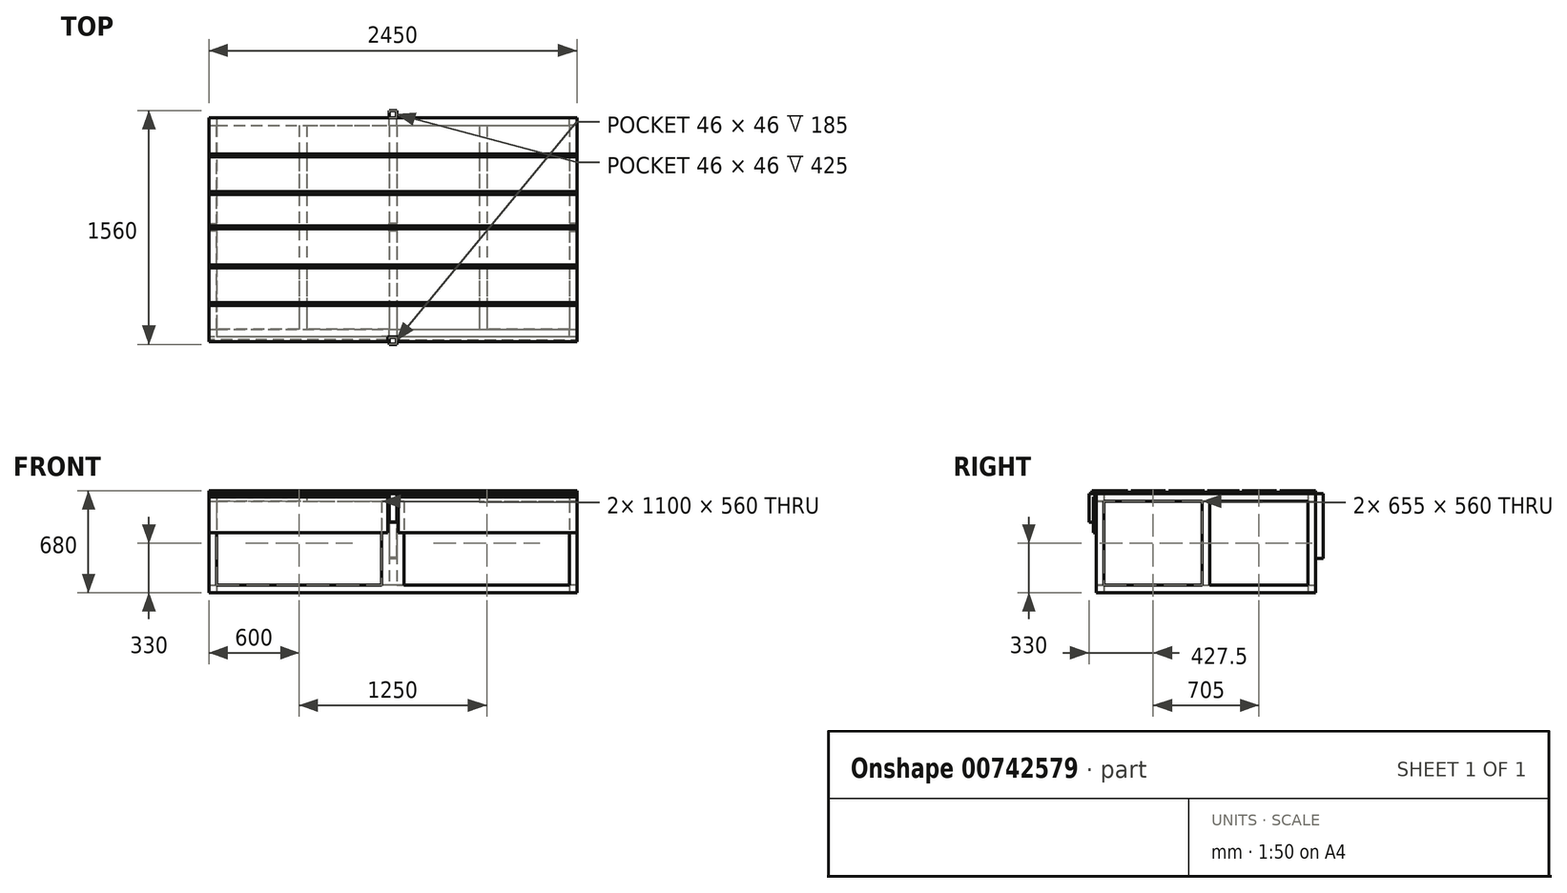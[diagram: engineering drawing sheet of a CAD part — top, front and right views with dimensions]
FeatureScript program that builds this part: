
annotation { "Feature Type Name" : "Feature", "Feature Type Description" : "" }
export const myFeature = defineFeature(function(context is Context, id is Id, definition is map)
    precondition{}
    {
        {
            var Q0;
            Q0=qCreatedBy(makeId("Top.planeOp"),FACE);
            var sketch = newSketch(context, id + "F0", { "sketchPlane" : qUnion([Q0])});
            skLineSegment(sketch, "E0.bottom", {"start": v(1225, -730) * mm, "end": v(-1225, -730) * mm});
            skLineSegment(sketch, "E0.top", {"start": v(1225, 730) * mm, "end": v(-1225, 730) * mm});
            skLineSegment(sketch, "E0.left", {"start": v(1225, -730) * mm, "end": v(1225, 730) * mm});
            skLineSegment(sketch, "E0.right", {"start": v(-1225, -730) * mm, "end": v(-1225, 730) * mm});
            skPoint(sketch, "E0.middle", {"position": v(0, 0) * mm});
            skLineSegment(sketch, "E1.bottom", {"start": v(-1175, 680) * mm, "end": v(1175, 680) * mm});
            skLineSegment(sketch, "E1.top", {"start": v(-1175, -680) * mm, "end": v(1175, -680) * mm});
            skLineSegment(sketch, "E1.left", {"start": v(-1175, 680) * mm, "end": v(-1175, -680) * mm});
            skLineSegment(sketch, "E1.right", {"start": v(1175, 680) * mm, "end": v(1175, -680) * mm});
            skLineSegment(sketch, "E2.bottom", {"start": v(25, 680) * mm, "end": v(-25, 680) * mm});
            skLineSegment(sketch, "E2.top", {"start": v(25, -680) * mm, "end": v(-25, -680) * mm});
            skLineSegment(sketch, "E2.left", {"start": v(25, 680) * mm, "end": v(25, -680) * mm});
            skLineSegment(sketch, "E2.right", {"start": v(-25, 680) * mm, "end": v(-25, -680) * mm});
            skSolve(sketch);
        }
        {
            var Q0;
            Q0=qSketchRegion(id+"F0",true);
            var Q1;
            Q1=makeQuery(id+"F0.imprint","IMPRINT",FACE,{"disambiguationData":[TD([[makeQuery(id+"F0.imprint","IMPRINT",EDGE,{"derivedFrom":sQuery(id+"F0.wireOp",EDGE,"E2.bottom")}),1.0]])]});
            extrude(context, id + "F1", {"entities" : qUnion([Q0, Q1]), "depth" : 50 * mm, "offsetDistance" : 25 * mm});
        }
        {
            var Q0;
            Q0=makeQuery(id+"F1.opExtrude","CAP_FACE",FACE,{"disambiguationData":[OSD([sQuery(id+"F0.wireOp",EDGE,"E0.bottom"),sQuery(id+"F0.wireOp",EDGE,"E0.top"),sQuery(id+"F0.wireOp",EDGE,"E0.left"),sQuery(id+"F0.wireOp",EDGE,"E0.right"),sQuery(id+"F0.wireOp",EDGE,"E1.bottom"),sQuery(id+"F0.wireOp",EDGE,"E1.top"),sQuery(id+"F0.wireOp",EDGE,"E1.left"),sQuery(id+"F0.wireOp",EDGE,"E1.right"),sQuery(id+"F0.wireOp",EDGE,"E2.left"),sQuery(id+"F0.wireOp",EDGE,"E2.right")])],"isStart":false});
            var sketch = newSketch(context, id + "F2", { "sketchPlane" : qUnion([Q0])});
            skLineSegment(sketch, "E3.bottom", {"start": v(-1225, 730) * mm, "end": v(-1175, 730) * mm});
            skLineSegment(sketch, "E3.top", {"start": v(-1225, 680) * mm, "end": v(-1175, 680) * mm});
            skLineSegment(sketch, "E3.left", {"start": v(-1225, 730) * mm, "end": v(-1225, 680) * mm});
            skLineSegment(sketch, "E3.right", {"start": v(-1175, 730) * mm, "end": v(-1175, 680) * mm});
            skLineSegment(sketch, "E4", {"start": v(-25, 680) * mm, "end": v(-25, 730) * mm});
            skLineSegment(sketch, "E5", {"start": v(25, 680) * mm, "end": v(25, 730) * mm});
            skLineSegment(sketch, "E6", {"start": v(25, 730) * mm, "end": v(-25, 730) * mm});
            skLineSegment(sketch, "E7", {"start": v(-25, 680) * mm, "end": v(25, 680) * mm});
            skLineSegment(sketch, "E8", {"start": v(1175, 680) * mm, "end": v(1175, 730) * mm});
            skLineSegment(sketch, "E9", {"start": v(1175, 730) * mm, "end": v(1225, 730) * mm});
            skLineSegment(sketch, "E10", {"start": v(1225, 730) * mm, "end": v(1225, 680) * mm});
            skLineSegment(sketch, "E11", {"start": v(1225, 680) * mm, "end": v(1175, 680) * mm});
            skLineSegment(sketch, "E12", {"start": v(1175, -680) * mm, "end": v(1225, -680) * mm});
            skLineSegment(sketch, "E13", {"start": v(1225, -680) * mm, "end": v(1225, -730) * mm});
            skLineSegment(sketch, "E14", {"start": v(1225, -730) * mm, "end": v(1175, -730) * mm});
            skLineSegment(sketch, "E15", {"start": v(1175, -730) * mm, "end": v(1175, -680) * mm});
            skLineSegment(sketch, "E16", {"start": v(-25, -680) * mm, "end": v(25, -680) * mm});
            skLineSegment(sketch, "E17", {"start": v(25, -680) * mm, "end": v(25, -730) * mm});
            skLineSegment(sketch, "E18", {"start": v(25, -730) * mm, "end": v(-25, -730) * mm});
            skLineSegment(sketch, "E19", {"start": v(-25, -730) * mm, "end": v(-25, -680) * mm});
            skLineSegment(sketch, "E20", {"start": v(-1175, -680) * mm, "end": v(-1175, -730) * mm});
            skLineSegment(sketch, "E21", {"start": v(-1175, -730) * mm, "end": v(-1225, -730) * mm});
            skLineSegment(sketch, "E22", {"start": v(-1225, -730) * mm, "end": v(-1225, -680) * mm});
            skLineSegment(sketch, "E23", {"start": v(-1225, -680) * mm, "end": v(-1175, -680) * mm});
            skLineSegment(sketch, "E24.bottom", {"start": v(25, -25) * mm, "end": v(-25, -25) * mm});
            skLineSegment(sketch, "E24.top", {"start": v(25, 25) * mm, "end": v(-25, 25) * mm});
            skLineSegment(sketch, "E24.left", {"start": v(25, -25) * mm, "end": v(25, 25) * mm});
            skLineSegment(sketch, "E24.right", {"start": v(-25, -25) * mm, "end": v(-25, 25) * mm});
            skPoint(sketch, "E24.middle", {"position": v(0, 0) * mm});
            skLineSegment(sketch, "E25", {"start": v(0, 0) * mm, "end": v(-1225, 0) * mm});
            skLineSegment(sketch, "E26", {"start": v(-1225, 25) * mm, "end": v(-1175, 25) * mm});
            skLineSegment(sketch, "E27", {"start": v(-1175, 25) * mm, "end": v(-1175, -25) * mm});
            skLineSegment(sketch, "E28", {"start": v(-1175, -25) * mm, "end": v(-1225, -25) * mm});
            skLineSegment(sketch, "E29", {"start": v(-1225, 25) * mm, "end": v(-1225, -25) * mm});
            skLineSegment(sketch, "E30.MirrorCS", {"start": v(1225, 25) * mm, "end": v(1225, -25) * mm});
            skLineSegment(sketch, "E31.MirrorCS", {"start": v(1175, -25) * mm, "end": v(1225, -25) * mm});
            skLineSegment(sketch, "E32.MirrorCS", {"start": v(1225, 25) * mm, "end": v(1175, 25) * mm});
            skLineSegment(sketch, "E33.MirrorCS", {"start": v(1175, 25) * mm, "end": v(1175, -25) * mm});
            skSolve(sketch);
        }
        {
            var Q0;
            Q0=qSketchRegion(id+"F2",true);
            extrude(context, id + "F3", {"entities" : qUnion([Q0]), "operationType" : NewBodyOperationType.ADD, "depth" : 560 * mm, "offsetDistance" : 25 * mm});
        }
        {
            var Q0;
            Q0=makeQuery(id+"F3.opExtrude","CAP_FACE",FACE,{"disambiguationData":[OSD([sQuery(id+"F2.wireOp",EDGE,"E26"),sQuery(id+"F2.wireOp",EDGE,"E27"),sQuery(id+"F2.wireOp",EDGE,"E28"),sQuery(id+"F2.wireOp",EDGE,"E29")])],"isStart":false});
            var sketch = newSketch(context, id + "F4", { "sketchPlane" : qUnion([Q0])});
            skLineSegment(sketch, "E34", {"start": v(-1225, 25) * mm, "end": v(-1225, 730) * mm});
            skLineSegment(sketch, "E35", {"start": v(-1225, 730) * mm, "end": v(-1175, 730) * mm});
            skLineSegment(sketch, "E36", {"start": v(-1175, 730) * mm, "end": v(1225, 730) * mm});
            skLineSegment(sketch, "E37", {"start": v(1225, 730) * mm, "end": v(1225, -730) * mm});
            skLineSegment(sketch, "E38", {"start": v(1225, -730) * mm, "end": v(-1225, -730) * mm});
            skLineSegment(sketch, "E39", {"start": v(-1225, -730) * mm, "end": v(-1225, 25) * mm});
            skLineSegment(sketch, "E40", {"start": v(-1175, 730) * mm, "end": v(-1175, 680) * mm});
            skLineSegment(sketch, "E41", {"start": v(-1175, 680) * mm, "end": v(-25, 680) * mm});
            skLineSegment(sketch, "E42", {"start": v(-1175, 680) * mm, "end": v(-600, 680) * mm});
            skLineSegment(sketch, "E43", {"start": v(-600, 680) * mm, "end": v(-575, 680) * mm});
            skLineSegment(sketch, "E44", {"start": v(-600, 680) * mm, "end": v(-625, 680) * mm});
            skLineSegment(sketch, "E45", {"start": v(-625, 680) * mm, "end": v(-625, -680) * mm});
            skLineSegment(sketch, "E46.MirrorCS", {"start": v(-575, 680) * mm, "end": v(-575, -680) * mm});
            skLineSegment(sketch, "E47", {"start": v(-25, 680) * mm, "end": v(25, 680) * mm});
            skLineSegment(sketch, "E48", {"start": v(25, 680) * mm, "end": v(1175, 680) * mm});
            skLineSegment(sketch, "E49", {"start": v(25, 680) * mm, "end": v(600, 680) * mm});
            skLineSegment(sketch, "E50", {"start": v(600, 680) * mm, "end": v(575, 680) * mm});
            skLineSegment(sketch, "E51", {"start": v(575, 680) * mm, "end": v(575, -680) * mm});
            skLineSegment(sketch, "E52.MirrorCS", {"start": v(625, 680) * mm, "end": v(625, -680) * mm});
            skLineSegment(sketch, "E53", {"start": v(-25, 680) * mm, "end": v(-25, -680) * mm});
            skLineSegment(sketch, "E54", {"start": v(-25, -680) * mm, "end": v(-575, -680) * mm});
            skLineSegment(sketch, "E55", {"start": v(-625, -680) * mm, "end": v(-1175, -680) * mm});
            skLineSegment(sketch, "E56", {"start": v(-1175, -680) * mm, "end": v(-1175, 680) * mm});
            skLineSegment(sketch, "E57", {"start": v(1175, 680) * mm, "end": v(1175, -680) * mm});
            skLineSegment(sketch, "E58", {"start": v(1175, -680) * mm, "end": v(625, -680) * mm});
            skLineSegment(sketch, "E59", {"start": v(25, 680) * mm, "end": v(25, -680) * mm});
            skLineSegment(sketch, "E60", {"start": v(25, -680) * mm, "end": v(575, -680) * mm});
            skSolve(sketch);
        }
        {
            var Q0;
            Q0=qSketchRegion(id+"F4",true);
            extrude(context, id + "F5", {"entities" : qUnion([Q0]), "operationType" : NewBodyOperationType.ADD, "depth" : 50 * mm, "offsetDistance" : 25 * mm});
        }
        {
            var Q0;
            {var subQ5=sQuery(id+"F0.wireOp",EDGE,"E1.left");var subQ6=sQuery(id+"F0.wireOp",EDGE,"E1.top");var subQ8=makeQuery(id+"F1.opExtrude","CAP_EDGE",EDGE,{"disambiguationData":[OSD([subQ6]),TDD([makeQuery(id+"F0.imprint","IMPRINT",EDGE,{"disambiguationData":[TD([[makeQuery(id+"F0.imprint","INTERSECT",VERTEX,{"derivedFrom":[subQ6,subQ5]}),-1.0]])],"derivedFrom":subQ6})])],"isStart":false});Q0=makeQuery(id+"F2.imprint","IMPRINT",FACE,{"disambiguationData":[TD([[makeQuery(id+"F2.imprint","IMPRINT",EDGE,{"derivedFrom":subQ8}),1.0]])]});}
            cPlane(context, id + "F6", {"entities" : qUnion([Q0]), "cplaneType" : CPlaneType.OFFSET, "offset" : 420 * mm, "width" : 150 * mm, "height" : 150 * mm});
        }
        {
            var Q0;
            Q0=qCreatedBy(id+"F6.planeOp",FACE);
            var sketch = newSketch(context, id + "F7", { "sketchPlane" : qUnion([Q0])});
            skLineSegment(sketch, "E61.bottom", {"start": v(-25, -730) * mm, "end": v(25, -730) * mm});
            skLineSegment(sketch, "E61.top", {"start": v(-25, -780) * mm, "end": v(25, -780) * mm});
            skLineSegment(sketch, "E61.left", {"start": v(-25, -730) * mm, "end": v(-25, -780) * mm});
            skLineSegment(sketch, "E61.right", {"start": v(25, -730) * mm, "end": v(25, -780) * mm});
            skSolve(sketch);
        }
        {
            var Q0;
            Q0=qSketchRegion(id+"F7",true);
            extrude(context, id + "F8", {"entities" : qUnion([Q0]), "operationType" : NewBodyOperationType.ADD, "depth" : 5 * mm, "offsetDistance" : 25 * mm});
        }
        {
            var Q0;
            Q0=makeQuery(id+"F8.opExtrude","CAP_FACE",FACE,{"disambiguationData":[OSD([sQuery(id+"F7.wireOp",EDGE,"E61.bottom"),sQuery(id+"F7.wireOp",EDGE,"E61.top"),sQuery(id+"F7.wireOp",EDGE,"E61.left"),sQuery(id+"F7.wireOp",EDGE,"E61.right")])],"isStart":false});
            var sketch = newSketch(context, id + "F9", { "sketchPlane" : qUnion([Q0])});
            skLineSegment(sketch, "E62.bottom", {"start": v(-25, -730) * mm, "end": v(25, -730) * mm});
            skLineSegment(sketch, "E62.top", {"start": v(-25, -780) * mm, "end": v(25, -780) * mm});
            skLineSegment(sketch, "E62.left", {"start": v(-25, -730) * mm, "end": v(-25, -780) * mm});
            skLineSegment(sketch, "E62.right", {"start": v(25, -730) * mm, "end": v(25, -780) * mm});
            skLineSegment(sketch, "E63.bottom", {"start": v(25, -780) * mm, "end": v(23, -780) * mm});
            skLineSegment(sketch, "E63.top", {"start": v(25, -778) * mm, "end": v(23, -778) * mm});
            skLineSegment(sketch, "E63.left", {"start": v(25, -780) * mm, "end": v(25, -778) * mm});
            skLineSegment(sketch, "E63.right", {"start": v(23, -780) * mm, "end": v(23, -778) * mm});
            skLineSegment(sketch, "E64.bottom", {"start": v(23, -778) * mm, "end": v(-23, -778) * mm});
            skLineSegment(sketch, "E64.top", {"start": v(23, -732) * mm, "end": v(-23, -732) * mm});
            skLineSegment(sketch, "E64.left", {"start": v(23, -778) * mm, "end": v(23, -732) * mm});
            skLineSegment(sketch, "E64.right", {"start": v(-23, -778) * mm, "end": v(-23, -732) * mm});
            skSolve(sketch);
        }
        {
            var Q0;
            Q0=qSketchRegion(id+"F9",true);
            var Q1;
            {var subQ0=sQuery(id+"F4.wireOp",EDGE,"E60");var subQ1=sQuery(id+"F4.wireOp",EDGE,"E59");var subQ2=sQuery(id+"F4.wireOp",EDGE,"E58");var subQ3=sQuery(id+"F4.wireOp",EDGE,"E57");var subQ4=sQuery(id+"F4.wireOp",EDGE,"E56");var subQ5=sQuery(id+"F4.wireOp",EDGE,"E55");var subQ6=sQuery(id+"F4.wireOp",EDGE,"E54");var subQ7=sQuery(id+"F4.wireOp",EDGE,"E53");var subQ8=sQuery(id+"F4.wireOp",EDGE,"E52.MirrorCS");var subQ9=sQuery(id+"F4.wireOp",EDGE,"E51");var subQ10=sQuery(id+"F4.wireOp",EDGE,"E49");var subQ11=sQuery(id+"F4.wireOp",EDGE,"E48");var subQ12=sQuery(id+"F4.wireOp",EDGE,"E46.MirrorCS");var subQ13=sQuery(id+"F4.wireOp",EDGE,"E45");var subQ14=sQuery(id+"F4.wireOp",EDGE,"E42");var subQ15=sQuery(id+"F4.wireOp",EDGE,"E41");var subQ16=sQuery(id+"F4.wireOp",EDGE,"E39");var subQ17=sQuery(id+"F4.wireOp",EDGE,"E38");var subQ18=sQuery(id+"F4.wireOp",EDGE,"E37");var subQ19=sQuery(id+"F4.wireOp",EDGE,"E36");var subQ20=sQuery(id+"F4.wireOp",EDGE,"E35");var subQ21=sQuery(id+"F4.wireOp",EDGE,"E34");Q1=makeQuery(id+"FP4IzDu3Lu8PIDH_1.boolean.opBoolean","MERGE",FACE,{"derivedFrom":[makeQuery(id+"F5.opExtrude","CAP_FACE",FACE,{"disambiguationData":[OSD([subQ21,subQ20,subQ19,subQ18,subQ17,subQ16,subQ15,subQ14,subQ13,subQ12,subQ11,subQ10,subQ9,subQ8,subQ7,subQ6,subQ5,subQ4,subQ3,subQ2,subQ1,subQ0])],"isStart":false}),makeQuery(id+"FP4IzDu3Lu8PIDH_1.opExtrude","CAP_FACE",FACE,{"disambiguationData":[OSD([subQ21,subQ20,subQ19,subQ18,subQ17,subQ16,subQ15,subQ14,subQ13,subQ12,subQ11,subQ10,subQ9,subQ8,subQ7,subQ6,subQ5,subQ4,subQ3,subQ2,subQ1,subQ0])],"isStart":false})]});}
            extrude(context, id + "F10", {"entities" : qUnion([Q0]), "operationType" : NewBodyOperationType.ADD, "endBound" : BoundingType.UP_TO_SURFACE, "depth" : 25 * mm, "endBoundEntityFace" : qUnion([Q1]), "offsetDistance" : 25 * mm});
        }
        {
            var Q0;
            {var subQ5=sQuery(id+"F0.wireOp",EDGE,"E1.left");var subQ6=sQuery(id+"F0.wireOp",EDGE,"E1.top");var subQ8=makeQuery(id+"F1.opExtrude","CAP_EDGE",EDGE,{"disambiguationData":[OSD([subQ6]),TDD([makeQuery(id+"F0.imprint","IMPRINT",EDGE,{"disambiguationData":[TD([[makeQuery(id+"F0.imprint","INTERSECT",VERTEX,{"derivedFrom":[subQ6,subQ5]}),-1.0]])],"derivedFrom":subQ6})])],"isStart":false});Q0=makeQuery(id+"F2.imprint","IMPRINT",FACE,{"disambiguationData":[TD([[makeQuery(id+"F2.imprint","IMPRINT",EDGE,{"derivedFrom":subQ8}),1.0]])]});}
            cPlane(context, id + "F11", {"entities" : qUnion([Q0]), "cplaneType" : CPlaneType.OFFSET, "offset" : 180 * mm, "width" : 150 * mm, "height" : 150 * mm});
        }
        {
            var Q0;
            Q0=qCreatedBy(id+"F11.planeOp",FACE);
            var sketch = newSketch(context, id + "F12", { "sketchPlane" : qUnion([Q0])});
            skLineSegment(sketch, "E65.bottom", {"start": v(-25, 730) * mm, "end": v(25, 730) * mm});
            skLineSegment(sketch, "E65.top", {"start": v(-25, 780) * mm, "end": v(25, 780) * mm});
            skLineSegment(sketch, "E65.left", {"start": v(-25, 730) * mm, "end": v(-25, 780) * mm});
            skLineSegment(sketch, "E65.right", {"start": v(25, 730) * mm, "end": v(25, 780) * mm});
            skSolve(sketch);
        }
        {
            var Q0;
            Q0=makeQuery(id+"F12.imprint","IMPRINT",FACE,{"disambiguationData":[TD([[makeQuery(id+"F12.imprint","IMPRINT",EDGE,{"derivedFrom":sQuery(id+"F12.wireOp",EDGE,"E65.bottom")}),1.0]])]});
            extrude(context, id + "F13", {"entities" : qUnion([Q0]), "operationType" : NewBodyOperationType.ADD, "depth" : 5 * mm, "offsetDistance" : 25 * mm});
        }
        {
            var Q0;
            Q0=makeQuery(id+"F3.opExtrude","SWEPT_FACE",FACE,{"disambiguationData":[OSD([sQuery(id+"F2.wireOp",EDGE,"E17")])]});
            cPlane(context, id + "F14", {"entities" : qUnion([Q0]), "cplaneType" : CPlaneType.OFFSET, "offset" : 25 * mm, "oppositeDirection" : true, "width" : 150 * mm, "height" : 150 * mm});
        }
        {
            var Q0;
            Q0=qCreatedBy(id+"F14.planeOp",FACE);
            var sketch = newSketch(context, id + "F15", { "sketchPlane" : qUnion([Q0])});
            skLineSegment(sketch, "E66.bottom", {"start": v(-730, 610) * mm, "end": v(-725, 610) * mm});
            skLineSegment(sketch, "E66.top", {"start": v(-730, 50) * mm, "end": v(-725, 50) * mm});
            skLineSegment(sketch, "E66.left", {"start": v(-730, 610) * mm, "end": v(-730, 50) * mm});
            skLineSegment(sketch, "E66.right", {"start": v(-725, 610) * mm, "end": v(-725, 50) * mm});
            skLineSegment(sketch, "E67.bottom", {"start": v(730, 610) * mm, "end": v(725, 610) * mm});
            skLineSegment(sketch, "E67.top", {"start": v(730, 50) * mm, "end": v(725, 50) * mm});
            skLineSegment(sketch, "E67.left", {"start": v(730, 610) * mm, "end": v(730, 50) * mm});
            skLineSegment(sketch, "E67.right", {"start": v(725, 610) * mm, "end": v(725, 50) * mm});
            skSolve(sketch);
        }
        {
            var Q0;
            Q0=qSketchRegion(id+"F15",true);
            extrude(context, id + "F16", {"entities" : qUnion([Q0]), "operationType" : NewBodyOperationType.ADD, "depth" : 75 * mm, "offsetDistance" : 25 * mm, "hasSecondDirection" : true, "secondDirectionOppositeDirection" : true, "secondDirectionDepth" : 75 * mm});
        }
        {
            var Q0;
            Q0=makeQuery(id+"F13.opExtrude","CAP_FACE",FACE,{"disambiguationData":[OSD([sQuery(id+"F12.wireOp",EDGE,"E65.bottom"),sQuery(id+"F12.wireOp",EDGE,"E65.top"),sQuery(id+"F12.wireOp",EDGE,"E65.left"),sQuery(id+"F12.wireOp",EDGE,"E65.right")])],"isStart":false});
            var sketch = newSketch(context, id + "F17", { "sketchPlane" : qUnion([Q0])});
            skLineSegment(sketch, "E68.bottom", {"start": v(-25, 780) * mm, "end": v(25, 780) * mm});
            skLineSegment(sketch, "E68.top", {"start": v(-25, 730) * mm, "end": v(25, 730) * mm});
            skLineSegment(sketch, "E68.left", {"start": v(-25, 780) * mm, "end": v(-25, 730) * mm});
            skLineSegment(sketch, "E68.right", {"start": v(25, 780) * mm, "end": v(25, 730) * mm});
            skLineSegment(sketch, "E69.bottom", {"start": v(25, 730) * mm, "end": v(23, 730) * mm});
            skLineSegment(sketch, "E69.top", {"start": v(25, 732) * mm, "end": v(23, 732) * mm});
            skLineSegment(sketch, "E69.left", {"start": v(25, 730) * mm, "end": v(25, 732) * mm});
            skLineSegment(sketch, "E70.bottom", {"start": v(23, 732) * mm, "end": v(-23, 732) * mm});
            skLineSegment(sketch, "E70.top", {"start": v(23, 778) * mm, "end": v(-23, 778) * mm});
            skLineSegment(sketch, "E70.left", {"start": v(23, 732) * mm, "end": v(23, 778) * mm});
            skLineSegment(sketch, "E70.right", {"start": v(-23, 732) * mm, "end": v(-23, 778) * mm});
            skSolve(sketch);
        }
        {
            var Q0;
            Q0=qSketchRegion(id+"F17",true);
            var Q1;
            {var subQ0=sQuery(id+"F4.wireOp",EDGE,"E60");var subQ1=sQuery(id+"F4.wireOp",EDGE,"E59");var subQ2=sQuery(id+"F4.wireOp",EDGE,"E58");var subQ3=sQuery(id+"F4.wireOp",EDGE,"E57");var subQ4=sQuery(id+"F4.wireOp",EDGE,"E56");var subQ5=sQuery(id+"F4.wireOp",EDGE,"E55");var subQ6=sQuery(id+"F4.wireOp",EDGE,"E54");var subQ7=sQuery(id+"F4.wireOp",EDGE,"E53");var subQ8=sQuery(id+"F4.wireOp",EDGE,"E52.MirrorCS");var subQ9=sQuery(id+"F4.wireOp",EDGE,"E51");var subQ10=sQuery(id+"F4.wireOp",EDGE,"E49");var subQ11=sQuery(id+"F4.wireOp",EDGE,"E48");var subQ12=sQuery(id+"F4.wireOp",EDGE,"E46.MirrorCS");var subQ13=sQuery(id+"F4.wireOp",EDGE,"E45");var subQ14=sQuery(id+"F4.wireOp",EDGE,"E42");var subQ15=sQuery(id+"F4.wireOp",EDGE,"E41");var subQ16=sQuery(id+"F4.wireOp",EDGE,"E39");var subQ17=sQuery(id+"F4.wireOp",EDGE,"E38");var subQ18=sQuery(id+"F4.wireOp",EDGE,"E37");var subQ19=sQuery(id+"F4.wireOp",EDGE,"E36");var subQ20=sQuery(id+"F4.wireOp",EDGE,"E35");var subQ21=sQuery(id+"F4.wireOp",EDGE,"E34");Q1=makeQuery(id+"F10.boolean.opBoolean","MERGE",FACE,{"derivedFrom":[makeQuery(id+"F5.opExtrude","CAP_FACE",FACE,{"disambiguationData":[OSD([subQ21,subQ20,subQ19,subQ18,subQ17,subQ16,subQ15,subQ14,subQ13,subQ12,subQ11,subQ10,subQ9,subQ8,subQ7,subQ6,subQ5,subQ4,subQ3,subQ2,subQ1,subQ0])],"isStart":false}),makeQuery(id+"F10.opExtrude","CAP_FACE",FACE,{"disambiguationData":[OSD([subQ21,subQ20,subQ19,subQ18,subQ17,subQ16,subQ15,subQ14,subQ13,subQ12,subQ11,subQ10,subQ9,subQ8,subQ7,subQ6,subQ5,subQ4,subQ3,subQ2,subQ1,subQ0])],"isStart":false})]});}
            extrude(context, id + "F18", {"entities" : qUnion([Q0]), "operationType" : NewBodyOperationType.ADD, "endBound" : BoundingType.UP_TO_SURFACE, "depth" : 25 * mm, "endBoundEntityFace" : qUnion([Q1]), "offsetDistance" : 25 * mm});
        }
        {
            var Q0;
            {var subQ0=sQuery(id+"F4.wireOp",EDGE,"E60");var subQ1=sQuery(id+"F4.wireOp",EDGE,"E59");var subQ2=sQuery(id+"F4.wireOp",EDGE,"E58");var subQ3=sQuery(id+"F4.wireOp",EDGE,"E57");var subQ4=sQuery(id+"F4.wireOp",EDGE,"E56");var subQ5=sQuery(id+"F4.wireOp",EDGE,"E55");var subQ6=sQuery(id+"F4.wireOp",EDGE,"E54");var subQ7=sQuery(id+"F4.wireOp",EDGE,"E53");var subQ8=sQuery(id+"F4.wireOp",EDGE,"E52.MirrorCS");var subQ9=sQuery(id+"F4.wireOp",EDGE,"E51");var subQ10=sQuery(id+"F4.wireOp",EDGE,"E49");var subQ11=sQuery(id+"F4.wireOp",EDGE,"E48");var subQ12=sQuery(id+"F4.wireOp",EDGE,"E46.MirrorCS");var subQ13=sQuery(id+"F4.wireOp",EDGE,"E45");var subQ14=sQuery(id+"F4.wireOp",EDGE,"E42");var subQ15=sQuery(id+"F4.wireOp",EDGE,"E41");var subQ16=sQuery(id+"F4.wireOp",EDGE,"E39");var subQ17=sQuery(id+"F4.wireOp",EDGE,"E38");var subQ18=sQuery(id+"F4.wireOp",EDGE,"E37");var subQ19=sQuery(id+"F4.wireOp",EDGE,"E36");var subQ20=sQuery(id+"F4.wireOp",EDGE,"E35");var subQ21=sQuery(id+"F4.wireOp",EDGE,"E34");Q0=makeQuery(id+"F18.boolean.opBoolean","MERGE",FACE,{"derivedFrom":[makeQuery(id+"F10.boolean.opBoolean","MERGE",FACE,{"derivedFrom":[makeQuery(id+"F5.opExtrude","CAP_FACE",FACE,{"disambiguationData":[OSD([subQ21,subQ20,subQ19,subQ18,subQ17,subQ16,subQ15,subQ14,subQ13,subQ12,subQ11,subQ10,subQ9,subQ8,subQ7,subQ6,subQ5,subQ4,subQ3,subQ2,subQ1,subQ0])],"isStart":false}),makeQuery(id+"F10.opExtrude","CAP_FACE",FACE,{"disambiguationData":[OSD([subQ21,subQ20,subQ19,subQ18,subQ17,subQ16,subQ15,subQ14,subQ13,subQ12,subQ11,subQ10,subQ9,subQ8,subQ7,subQ6,subQ5,subQ4,subQ3,subQ2,subQ1,subQ0])],"isStart":false})]}),makeQuery(id+"F18.opExtrude","CAP_FACE",FACE,{"disambiguationData":[OSD([subQ21,subQ20,subQ19,subQ18,subQ17,subQ16,subQ15,subQ14,subQ13,subQ12,subQ11,subQ10,subQ9,subQ8,subQ7,subQ6,subQ5,subQ4,subQ3,subQ2,subQ1,subQ0])],"isStart":false})]});}
            var sketch = newSketch(context, id + "F19", { "sketchPlane" : qUnion([Q0])});
            skLineSegment(sketch, "E71.bottom", {"start": v(-1225, 730) * mm, "end": v(1225, 730) * mm});
            skLineSegment(sketch, "E71.top", {"start": v(-1225, -730) * mm, "end": v(1225, -730) * mm});
            skLineSegment(sketch, "E71.left", {"start": v(-1225, 730) * mm, "end": v(-1225, -730) * mm});
            skLineSegment(sketch, "E71.right", {"start": v(1225, 730) * mm, "end": v(1225, -730) * mm});
            skLineSegment(sketch, "E72", {"start": v(1225, -730) * mm, "end": v(1225, -760) * mm});
            skLineSegment(sketch, "E73.top", {"start": v(1225, -730) * mm, "end": v(46.2, -730) * mm});
            skLineSegment(sketch, "E73.left", {"start": v(1225, -760) * mm, "end": v(1225, -730) * mm});
            skLineSegment(sketch, "E74.top", {"start": v(46.2, -730) * mm, "end": v(-45, -730) * mm});
            skLineSegment(sketch, "E75.top", {"start": v(-45, -730) * mm, "end": v(-1225, -730) * mm});
            skLineSegment(sketch, "E75.right", {"start": v(-1225, -760) * mm, "end": v(-1225, -730) * mm});
            skLineSegment(sketch, "E76", {"start": v(35, -760) * mm, "end": v(35, -730) * mm});
            skLineSegment(sketch, "E77", {"start": v(-35, -760) * mm, "end": v(-35, -730) * mm});
            skLineSegment(sketch, "E78", {"start": v(35, -760) * mm, "end": v(1225, -760) * mm});
            skLineSegment(sketch, "E79", {"start": v(-1225, -760) * mm, "end": v(-35, -760) * mm});
            skSolve(sketch);
        }
        {
            var Q0;
            Q0=qSketchRegion(id+"F19",true);
            extrude(context, id + "F20", {"entities" : qUnion([Q0]), "depth" : 20 * mm, "offsetDistance" : 25 * mm});
        }
        {
            var Q0;
            Q0=makeQuery(id+"F16.boolean.opBoolean","MERGE",FACE,{"derivedFrom":[makeQuery(id+"F5.boolean.opBoolean","MERGE",FACE,{"derivedFrom":[makeQuery(id+"F3.boolean.opBoolean","MERGE",FACE,{"derivedFrom":[makeQuery(id+"F1.opExtrude","SWEPT_FACE",FACE,{"disambiguationData":[OSD([sQuery(id+"F0.wireOp",EDGE,"E0.bottom")])]}),makeQuery(id+"F3.opExtrude","SWEPT_FACE",FACE,{"disambiguationData":[OSD([sQuery(id+"F2.wireOp",EDGE,"E14")])]}),makeQuery(id+"F3.opExtrude","SWEPT_FACE",FACE,{"disambiguationData":[OSD([sQuery(id+"F2.wireOp",EDGE,"E18")])]}),makeQuery(id+"F3.opExtrude","SWEPT_FACE",FACE,{"disambiguationData":[OSD([sQuery(id+"F2.wireOp",EDGE,"E21")])]})]}),makeQuery(id+"F5.opExtrude","SWEPT_FACE",FACE,{"disambiguationData":[OSD([sQuery(id+"F4.wireOp",EDGE,"E38")])]})]}),makeQuery(id+"F16.opExtrude","SWEPT_FACE",FACE,{"disambiguationData":[OSD([sQuery(id+"F15.wireOp",EDGE,"E66.left")])]})]});
            var sketch = newSketch(context, id + "F21", { "sketchPlane" : qUnion([Q0])});
            skLineSegment(sketch, "E80", {"start": v(-25, 660) * mm, "end": v(-35, 660) * mm});
            skLineSegment(sketch, "E81", {"start": v(-35, 660) * mm, "end": v(-35, 640) * mm});
            skLineSegment(sketch, "E82", {"start": v(25, 660) * mm, "end": v(35, 660) * mm});
            skLineSegment(sketch, "E83", {"start": v(35, 660) * mm, "end": v(35, 640) * mm});
            skLineSegment(sketch, "E84.bottom", {"start": v(-35, 640) * mm, "end": v(-1225, 640) * mm});
            skLineSegment(sketch, "E84.top", {"start": v(-35, 400) * mm, "end": v(-1225, 400) * mm});
            skLineSegment(sketch, "E84.left", {"start": v(-35, 640) * mm, "end": v(-35, 400) * mm});
            skLineSegment(sketch, "E84.right", {"start": v(-1225, 640) * mm, "end": v(-1225, 400) * mm});
            skLineSegment(sketch, "E85.bottom", {"start": v(35, 640) * mm, "end": v(1225, 640) * mm});
            skLineSegment(sketch, "E85.top", {"start": v(35, 400) * mm, "end": v(1225, 400) * mm});
            skLineSegment(sketch, "E85.left", {"start": v(35, 640) * mm, "end": v(35, 400) * mm});
            skLineSegment(sketch, "E85.right", {"start": v(1225, 640) * mm, "end": v(1225, 400) * mm});
            skSolve(sketch);
        }
        {
            var Q0;
            Q0=qSketchRegion(id+"F21",true);
            extrude(context, id + "F22", {"entities" : qUnion([Q0]), "depth" : 20 * mm, "offsetDistance" : 25 * mm});
        }
        {
            var Q0;
            Q0=makeQuery(id+"F20.opExtrude","SWEPT_FACE",FACE,{"disambiguationData":[OSD([sQuery(id+"F19.wireOp",EDGE,"E71.left"),sQuery(id+"F19.wireOp",EDGE,"E75.right")])]});
            var sketch = newSketch(context, id + "F23", { "sketchPlane" : qUnion([Q0])});
            skLineSegment(sketch, "E86", {"start": v(730, 680) * mm, "end": v(10, 680) * mm});
            skLineSegment(sketch, "E87.bottom", {"start": v(10, 680) * mm, "end": v(-10, 680) * mm});
            skLineSegment(sketch, "E87.top", {"start": v(10, 660) * mm, "end": v(-10, 660) * mm});
            skLineSegment(sketch, "E87.left", {"start": v(10, 680) * mm, "end": v(10, 660) * mm});
            skLineSegment(sketch, "E87.right", {"start": v(-10, 680) * mm, "end": v(-10, 660) * mm});
            skLineSegment(sketch, "E88", {"start": v(-10, 680) * mm, "end": v(-160.18, 680) * mm});
            skLineSegment(sketch, "E89", {"start": v(730, 680) * mm, "end": v(520, 680) * mm});
            skLineSegment(sketch, "E90.bottom", {"start": v(520, 680) * mm, "end": v(500, 680) * mm});
            skLineSegment(sketch, "E90.top", {"start": v(520, 660) * mm, "end": v(500, 660) * mm});
            skLineSegment(sketch, "E90.left", {"start": v(520, 680) * mm, "end": v(520, 660) * mm});
            skLineSegment(sketch, "E90.right", {"start": v(500, 680) * mm, "end": v(500, 660) * mm});
            skLineSegment(sketch, "E91", {"start": v(500, 680) * mm, "end": v(270, 680) * mm});
            skLineSegment(sketch, "E92.bottom", {"start": v(270, 680) * mm, "end": v(250, 680) * mm});
            skLineSegment(sketch, "E92.top", {"start": v(270, 660) * mm, "end": v(250, 660) * mm});
            skLineSegment(sketch, "E92.left", {"start": v(270, 680) * mm, "end": v(270, 660) * mm});
            skLineSegment(sketch, "E92.right", {"start": v(250, 680) * mm, "end": v(250, 660) * mm});
            skLineSegment(sketch, "E93", {"start": v(-10, 680) * mm, "end": v(-220, 680) * mm});
            skLineSegment(sketch, "E94.bottom", {"start": v(-220, 680) * mm, "end": v(-240, 680) * mm});
            skLineSegment(sketch, "E94.top", {"start": v(-220, 660) * mm, "end": v(-240, 660) * mm});
            skLineSegment(sketch, "E94.left", {"start": v(-220, 680) * mm, "end": v(-220, 660) * mm});
            skLineSegment(sketch, "E94.right", {"start": v(-240, 680) * mm, "end": v(-240, 660) * mm});
            skLineSegment(sketch, "E95", {"start": v(-240, 680) * mm, "end": v(-470, 680) * mm});
            skLineSegment(sketch, "E96.bottom", {"start": v(-470, 680) * mm, "end": v(-490, 680) * mm});
            skLineSegment(sketch, "E96.top", {"start": v(-470, 660) * mm, "end": v(-490, 660) * mm});
            skLineSegment(sketch, "E96.left", {"start": v(-470, 680) * mm, "end": v(-470, 660) * mm});
            skLineSegment(sketch, "E96.right", {"start": v(-490, 680) * mm, "end": v(-490, 660) * mm});
            skLineSegment(sketch, "E97", {"start": v(730, 660) * mm, "end": v(730, 680) * mm});
            skSolve(sketch);
        }
        {
            var Q0;
            Q0 = qSketchRegion(id + "F23", true);
            var Q1;
            Q1=makeQuery(id+"F20.opExtrude","SWEPT_FACE",FACE,{"disambiguationData":[OSD([sQuery(id+"F19.wireOp",EDGE,"E71.right"),sQuery(id+"F19.wireOp",EDGE,"E73.left")])]});
            extrude(context, id + "F24", {"entities" : qUnion([Q0]), "operationType" : NewBodyOperationType.REMOVE, "endBound" : BoundingType.UP_TO_SURFACE, "oppositeDirection" : true, "depth" : 25 * mm, "endBoundEntityFace" : qUnion([Q1]), "offsetDistance" : 25 * mm});
        }
    });
